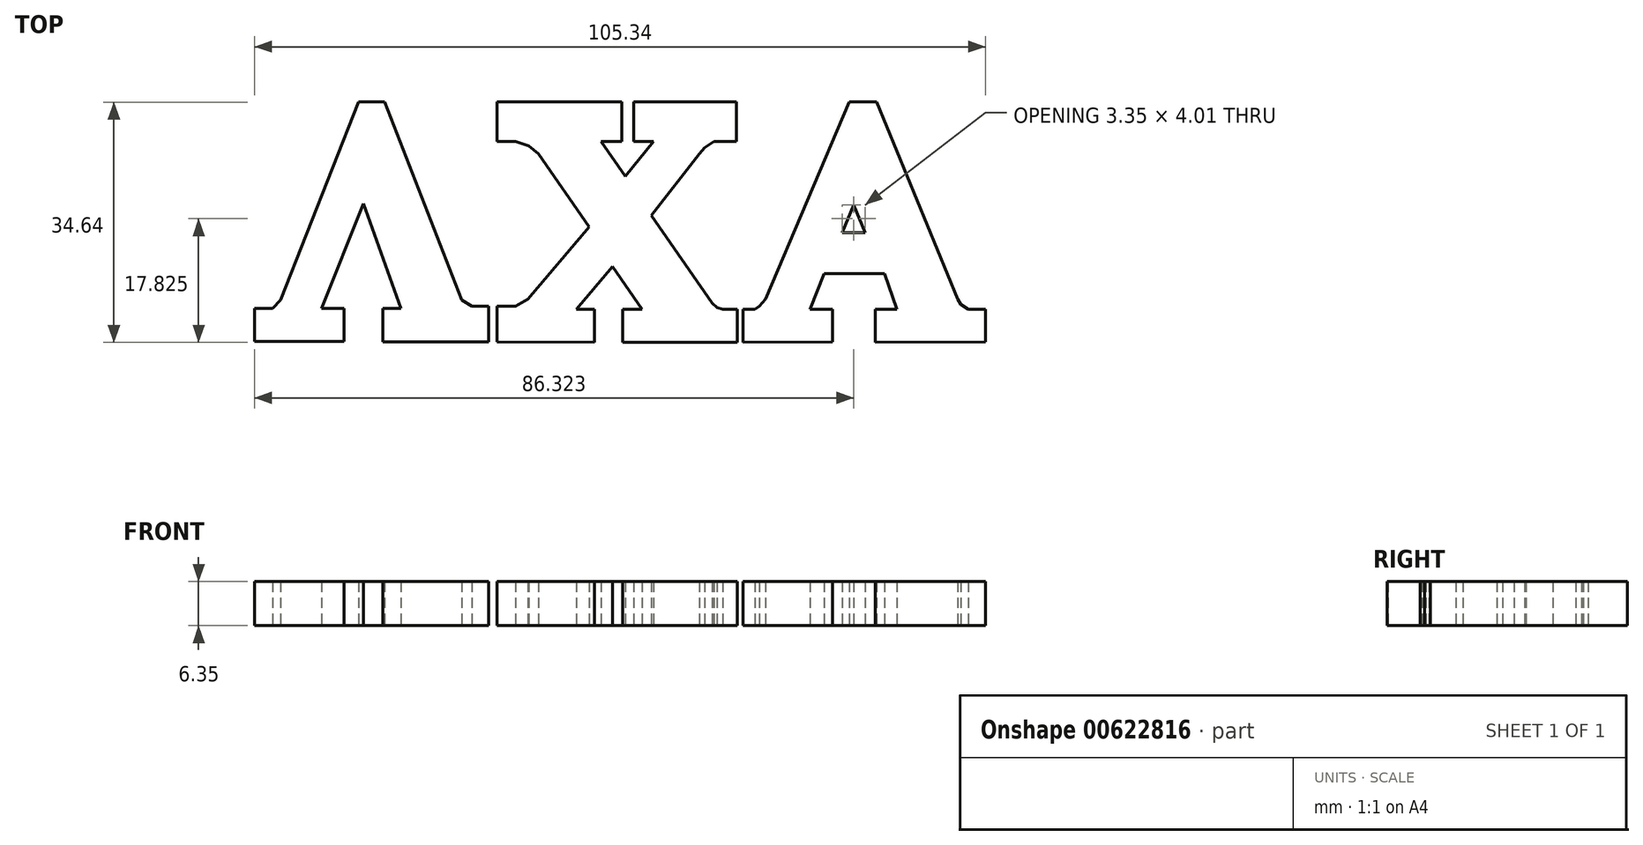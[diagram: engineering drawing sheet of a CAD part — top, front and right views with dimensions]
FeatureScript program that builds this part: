
annotation { "Feature Type Name" : "Feature", "Feature Type Description" : "" }
export const myFeature = defineFeature(function(context is Context, id is Id, definition is map)
    precondition{}
    {
        {
            var Q0;
            Q0=qCreatedBy(makeId("Top.planeOp"),FACE);
            var sketch = newSketch(context, id + "F0", { "sketchPlane" : qUnion([Q0])});
            skLineSegment(sketch, "E0", {"start": v(-39.95, 21.4) * mm, "end": v(-36.16, 21.4) * mm});
            skLineSegment(sketch, "E1", {"start": v(-36.16, 21.4) * mm, "end": v(-25.09, -7.16) * mm});
            skLineSegment(sketch, "E2", {"start": v(-25.09, -7.16) * mm, "end": v(-23.59, -8.05) * mm});
            skLineSegment(sketch, "E3", {"start": v(-23.59, -8.05) * mm, "end": v(-21.18, -8.05) * mm});
            skLineSegment(sketch, "E4", {"start": v(-21.18, -8.05) * mm, "end": v(-21.18, -13.2) * mm});
            skLineSegment(sketch, "E5", {"start": v(-21.18, -13.2) * mm, "end": v(-36.41, -13.2) * mm});
            skLineSegment(sketch, "E6", {"start": v(-36.41, -13.2) * mm, "end": v(-36.41, -8.36) * mm});
            skLineSegment(sketch, "E7", {"start": v(-36.41, -8.36) * mm, "end": v(-33.86, -8.36) * mm});
            skLineSegment(sketch, "E8", {"start": v(-33.86, -8.36) * mm, "end": v(-39.25, 6.77) * mm});
            skLineSegment(sketch, "E9", {"start": v(-39.25, 6.77) * mm, "end": v(-45.28, -8.36) * mm});
            skLineSegment(sketch, "E10", {"start": v(-45.28, -8.36) * mm, "end": v(-42.06, -8.36) * mm});
            skLineSegment(sketch, "E11", {"start": v(-42.06, -8.36) * mm, "end": v(-42.06, -13.1) * mm});
            skLineSegment(sketch, "E12", {"start": v(-42.06, -13.1) * mm, "end": v(-54.95, -13.1) * mm});
            skLineSegment(sketch, "E13", {"start": v(-54.95, -13.1) * mm, "end": v(-54.95, -8.36) * mm});
            skLineSegment(sketch, "E14", {"start": v(-54.95, -8.36) * mm, "end": v(-52.32, -8.36) * mm});
            skLineSegment(sketch, "E15", {"start": v(-52.32, -8.36) * mm, "end": v(-51.17, -7.13) * mm});
            skLineSegment(sketch, "E16", {"start": v(-51.17, -7.13) * mm, "end": v(-39.95, 21.4) * mm});
            skLineSegment(sketch, "E17", {"start": v(-19.98, -13.2) * mm, "end": v(-19.98, -8.05) * mm});
            skLineSegment(sketch, "E18", {"start": v(-19.98, -8.05) * mm, "end": v(-17.36, -8.05) * mm});
            skLineSegment(sketch, "E19", {"start": v(-17.36, -8.05) * mm, "end": v(-15.54, -6.99) * mm});
            skLineSegment(sketch, "E20", {"start": v(-15.54, -6.99) * mm, "end": v(-6.74, 3.4) * mm});
            skLineSegment(sketch, "E21", {"start": v(-6.74, 3.4) * mm, "end": v(-14.05, 13.96) * mm});
            skLineSegment(sketch, "E22", {"start": v(-14.05, 13.96) * mm, "end": v(-15.4, 15.06) * mm});
            skLineSegment(sketch, "E23", {"start": v(-15.4, 15.06) * mm, "end": v(-17.32, 15.72) * mm});
            skLineSegment(sketch, "E24", {"start": v(-17.32, 15.72) * mm, "end": v(-19.98, 15.72) * mm});
            skLineSegment(sketch, "E25", {"start": v(-2, 15.72) * mm, "end": v(-5, 15.72) * mm});
            skLineSegment(sketch, "E26", {"start": v(-5, 15.72) * mm, "end": v(-1.53, 10.67) * mm});
            skLineSegment(sketch, "E27", {"start": v(-1.53, 10.67) * mm, "end": v(2.58, 15.72) * mm});
            skLineSegment(sketch, "E28", {"start": v(2.58, 15.72) * mm, "end": v(-0.32, 15.72) * mm});
            skLineSegment(sketch, "E29", {"start": v(14.46, 15.72) * mm, "end": v(11.26, 15.72) * mm});
            skLineSegment(sketch, "E30", {"start": v(11.26, 15.72) * mm, "end": v(9.9, 14.8) * mm});
            skLineSegment(sketch, "E31", {"start": v(9.9, 14.8) * mm, "end": v(9.13, 13.95) * mm});
            skLineSegment(sketch, "E32", {"start": v(9.13, 13.95) * mm, "end": v(2.25, 5.08) * mm});
            skLineSegment(sketch, "E33", {"start": v(2.25, 5.08) * mm, "end": v(10.96, -7.6) * mm});
            skLineSegment(sketch, "E34", {"start": v(10.96, -7.6) * mm, "end": v(11.7, -8.24) * mm});
            skLineSegment(sketch, "E35", {"start": v(11.7, -8.24) * mm, "end": v(12.5, -8.47) * mm});
            skLineSegment(sketch, "E36", {"start": v(12.5, -8.47) * mm, "end": v(14.59, -8.47) * mm});
            skLineSegment(sketch, "E37", {"start": v(14.59, -8.47) * mm, "end": v(14.59, -13.24) * mm});
            skLineSegment(sketch, "E38", {"start": v(14.59, -13.24) * mm, "end": v(-1.88, -13.24) * mm});
            skLineSegment(sketch, "E39", {"start": v(-1.88, -13.24) * mm, "end": v(-1.88, -8.47) * mm});
            skLineSegment(sketch, "E40", {"start": v(-1.88, -8.47) * mm, "end": v(0.9, -8.47) * mm});
            skLineSegment(sketch, "E41", {"start": v(0.9, -8.47) * mm, "end": v(-3.34, -2.3) * mm});
            skLineSegment(sketch, "E42", {"start": v(-3.34, -2.3) * mm, "end": v(-8.57, -8.47) * mm});
            skLineSegment(sketch, "E43", {"start": v(-8.57, -8.47) * mm, "end": v(-5.99, -8.47) * mm});
            skLineSegment(sketch, "E44", {"start": v(-5.99, -8.47) * mm, "end": v(-5.99, -13.24) * mm});
            skLineSegment(sketch, "E45", {"start": v(-5.99, -13.24) * mm, "end": v(-19.98, -13.2) * mm});
            skLineSegment(sketch, "E46", {"start": v(25.08, -8.47) * mm, "end": v(28.35, -8.47) * mm});
            skLineSegment(sketch, "E47", {"start": v(28.35, -8.47) * mm, "end": v(28.35, -13.2) * mm});
            skLineSegment(sketch, "E48", {"start": v(28.35, -13.2) * mm, "end": v(15.45, -13.24) * mm});
            skLineSegment(sketch, "E49", {"start": v(15.45, -13.24) * mm, "end": v(15.45, -8.47) * mm});
            skLineSegment(sketch, "E50", {"start": v(15.45, -8.47) * mm, "end": v(17.17, -8.47) * mm});
            skLineSegment(sketch, "E51", {"start": v(17.17, -8.47) * mm, "end": v(17.78, -8.05) * mm});
            skLineSegment(sketch, "E52", {"start": v(17.78, -8.05) * mm, "end": v(18.68, -6.99) * mm});
            skLineSegment(sketch, "E53", {"start": v(18.68, -6.99) * mm, "end": v(30.74, 21.4) * mm});
            skPoint(sketch, "E53.endSnap0", {"position": v(-38.06, 21.4) * mm});
            skLineSegment(sketch, "E54", {"start": v(30.74, 21.4) * mm, "end": v(34.66, 21.4) * mm});
            skLineSegment(sketch, "E55", {"start": v(34.66, 21.4) * mm, "end": v(46.34, -6.99) * mm});
            skLineSegment(sketch, "E56", {"start": v(46.34, -6.99) * mm, "end": v(46.81, -7.8) * mm});
            skLineSegment(sketch, "E57", {"start": v(46.81, -7.8) * mm, "end": v(47.87, -8.47) * mm});
            skLineSegment(sketch, "E58", {"start": v(47.87, -8.47) * mm, "end": v(50.38, -8.47) * mm});
            skLineSegment(sketch, "E59", {"start": v(50.38, -8.47) * mm, "end": v(50.4, -13.2) * mm});
            skLineSegment(sketch, "E60", {"start": v(50.4, -13.2) * mm, "end": v(34.48, -13.24) * mm});
            skLineSegment(sketch, "E61", {"start": v(34.48, -13.24) * mm, "end": v(34.48, -8.47) * mm});
            skLineSegment(sketch, "E62", {"start": v(34.48, -8.47) * mm, "end": v(37.61, -8.47) * mm});
            skLineSegment(sketch, "E63", {"start": v(37.61, -8.47) * mm, "end": v(35.8, -3.31) * mm});
            skLineSegment(sketch, "E64", {"start": v(35.8, -3.31) * mm, "end": v(27.14, -3.31) * mm});
            skLineSegment(sketch, "E65", {"start": v(27.14, -3.31) * mm, "end": v(25.08, -8.47) * mm});
            skLineSegment(sketch, "E66", {"start": v(31.4, 6.59) * mm, "end": v(29.7, 2.58) * mm});
            skLineSegment(sketch, "E67", {"start": v(31.4, 6.59) * mm, "end": v(33.05, 2.58) * mm});
            skLineSegment(sketch, "E68", {"start": v(33.05, 2.58) * mm, "end": v(29.7, 2.58) * mm});
            skLineSegment(sketch, "E69", {"start": v(-19.98, 15.72) * mm, "end": v(-19.98, 21.4) * mm});
            skPoint(sketch, "E69.endSnap0", {"position": v(32.7, 21.4) * mm});
            skLineSegment(sketch, "E70", {"start": v(-19.98, 21.4) * mm, "end": v(-2, 21.4) * mm});
            skLineSegment(sketch, "E71", {"start": v(-2, 21.4) * mm, "end": v(-2, 15.72) * mm});
            skLineSegment(sketch, "E72", {"start": v(-0.32, 15.72) * mm, "end": v(-0.32, 21.4) * mm});
            skLineSegment(sketch, "E73", {"start": v(-0.32, 21.4) * mm, "end": v(14.46, 21.4) * mm});
            skLineSegment(sketch, "E74", {"start": v(14.46, 21.4) * mm, "end": v(14.46, 15.72) * mm});
            skSolve(sketch);
        }
        {
            var Q0;
            Q0=makeQuery(id+"F0.imprint","IMPRINT",FACE,{"disambiguationData":[TD([[makeQuery(id+"F0.imprint","IMPRINT",EDGE,{"derivedFrom":sQuery(id+"F0.wireOp",EDGE,"E17")}),-1.0]])]});
            var Q1;
            Q1=makeQuery(id+"F0.imprint","IMPRINT",FACE,{"disambiguationData":[TD([[makeQuery(id+"F0.imprint","IMPRINT",EDGE,{"derivedFrom":sQuery(id+"F0.wireOp",EDGE,"E0")}),-1.0]])]});
            var Q2;
            Q2=makeQuery(id+"F0.imprint","IMPRINT",FACE,{"disambiguationData":[TD([[makeQuery(id+"F0.imprint","IMPRINT",EDGE,{"derivedFrom":sQuery(id+"F0.wireOp",EDGE,"E46")}),-1.0]])]});
            extrude(context, id + "F1", {"entities" : qUnion([Q0, Q1, Q2]), "depth" : 6.35 * mm, "offsetDistance" : 25.4 * mm});
        }
    });
